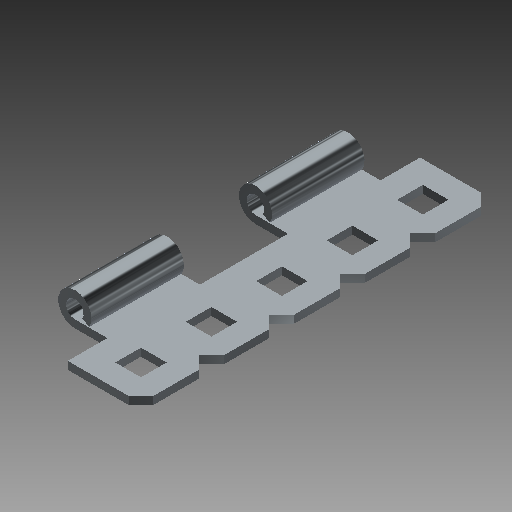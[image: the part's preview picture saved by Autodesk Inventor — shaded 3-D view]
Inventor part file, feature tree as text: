
AUTODESK INVENTOR PART (.ipt)
format: ipt  version: 2018 (Build 220112000, 112)  size: 210,432 bytes
history: native  units: in
note: dims shown in document units (in); Inventor stores cm internally (conversion verified against a paired STEP export)
features: extrude x7, other x5, sketch x3, pattern_linear x1
ambient origin geometry x8: Origin, YZ Plane, XZ Plane, XY Plane, X Axis, Y Axis, Z Axis, Center Point
bodies: Solid1 (feature_tree)
feature tree (16):
  extrude  "Extrusion1"  Depth=2.5in TaperAngle=0.0deg
  extrude  "Extrusion2"  Depth=0.5in
  pattern_linear  "Rectangular Pattern1"  Spacing1=0.0in  [1 undecoded]
  sketch  "Sketch1"  dims[d0=2.5in d1=0.0in d2=0.25in d3=0.0in]
  sketch  "Sketch2"  dims[d4=0.25in d5=0.0in d6=1.9685in d8=0.5in]
  sketch  "Sketch3"  dims[d9=0.0in d10=0.0in d11=0.0in d12=0.0in d13=0.0in d14=0.0in d15=0.0in d16=0.0in d17=0.0in d18=0.0in]
  other  "Srf1"
  other  "Srf2"
  other  "Srf3"
  other  "Srf4"
  other  "Srf5"
  extrude  "ExtrusionSrf1"  TaperAngle=0.0deg  [1 undecoded]
  extrude  "ExtrusionSrf2"  TaperAngle=0.0deg  [1 undecoded]
  extrude  "ExtrusionSrf3"  TaperAngle=0.0deg  [1 undecoded]
  extrude  "ExtrusionSrf4"  TaperAngle=0.0deg  [1 undecoded]
  extrude  "ExtrusionSrf5"  TaperAngle=0.0deg  [1 undecoded]
note: 6 required parameter values undecoded (feature->parameter linkage not recoverable at this tier; creation-order binding heuristic only, values carry confidence <= 0.55)
